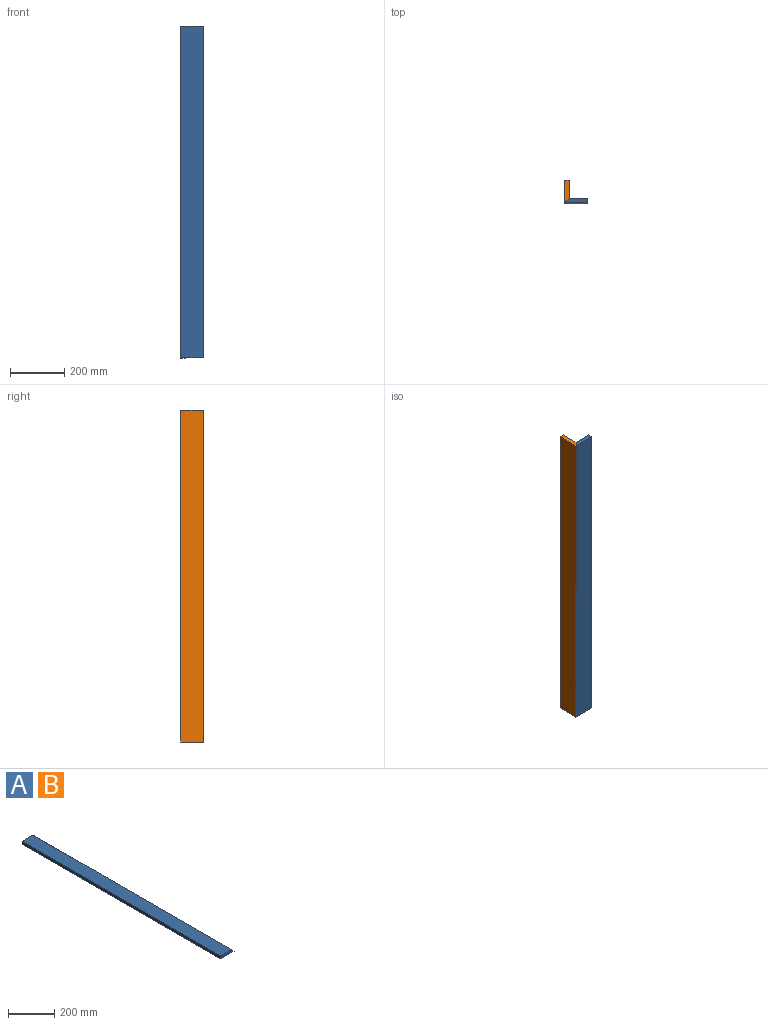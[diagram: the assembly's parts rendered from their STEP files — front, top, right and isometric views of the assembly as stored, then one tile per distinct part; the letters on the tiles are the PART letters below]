
ASSEMBLY  parts=2 mates=1
PART A: 6 faces, bbox 82.6x1219.2x15.9 mm
  f0: plane 82.55x15.88mm, normal (0,-1,0), area 1184.5mm2, adj f2,f3,f4,f5
  f1: plane 82.55x15.88mm, normal (0,1,0), area 1184.5mm2, adj f2,f3,f4,f5
  f2: plane 1219.2x15.88mm, normal (-1,0,0), area 19354.8mm2, adj f0,f1,f3,f4
  f3: plane 1219.2x82.55mm, normal (0,0,-1), area 100645mm2, adj f0,f1,f2,f5
  f4: plane 1219.2x66.68mm, normal (0,0,1), area 81290.2mm2, adj f0,f1,f2,f5
  f5: plane 1219.2x15.88mm, normal (0.71,0,0.71), area 27371.8mm2, adj f0,f1,f3,f4
PART B: same geometry as A
PLACE A rot(axis=(0,-0.71,-0.71),180deg) t=(256.35,-148.71,1249.15)mm
PLACE B rot(axis=(-0.58,0.58,-0.58),120deg) t=(173.8,-66.16,29.95)mm fixed
MATE fastened A.f5 <-> B.f5  axis (-0.71,0.71,0) through (181.73,-140.77,1249.15)mm
